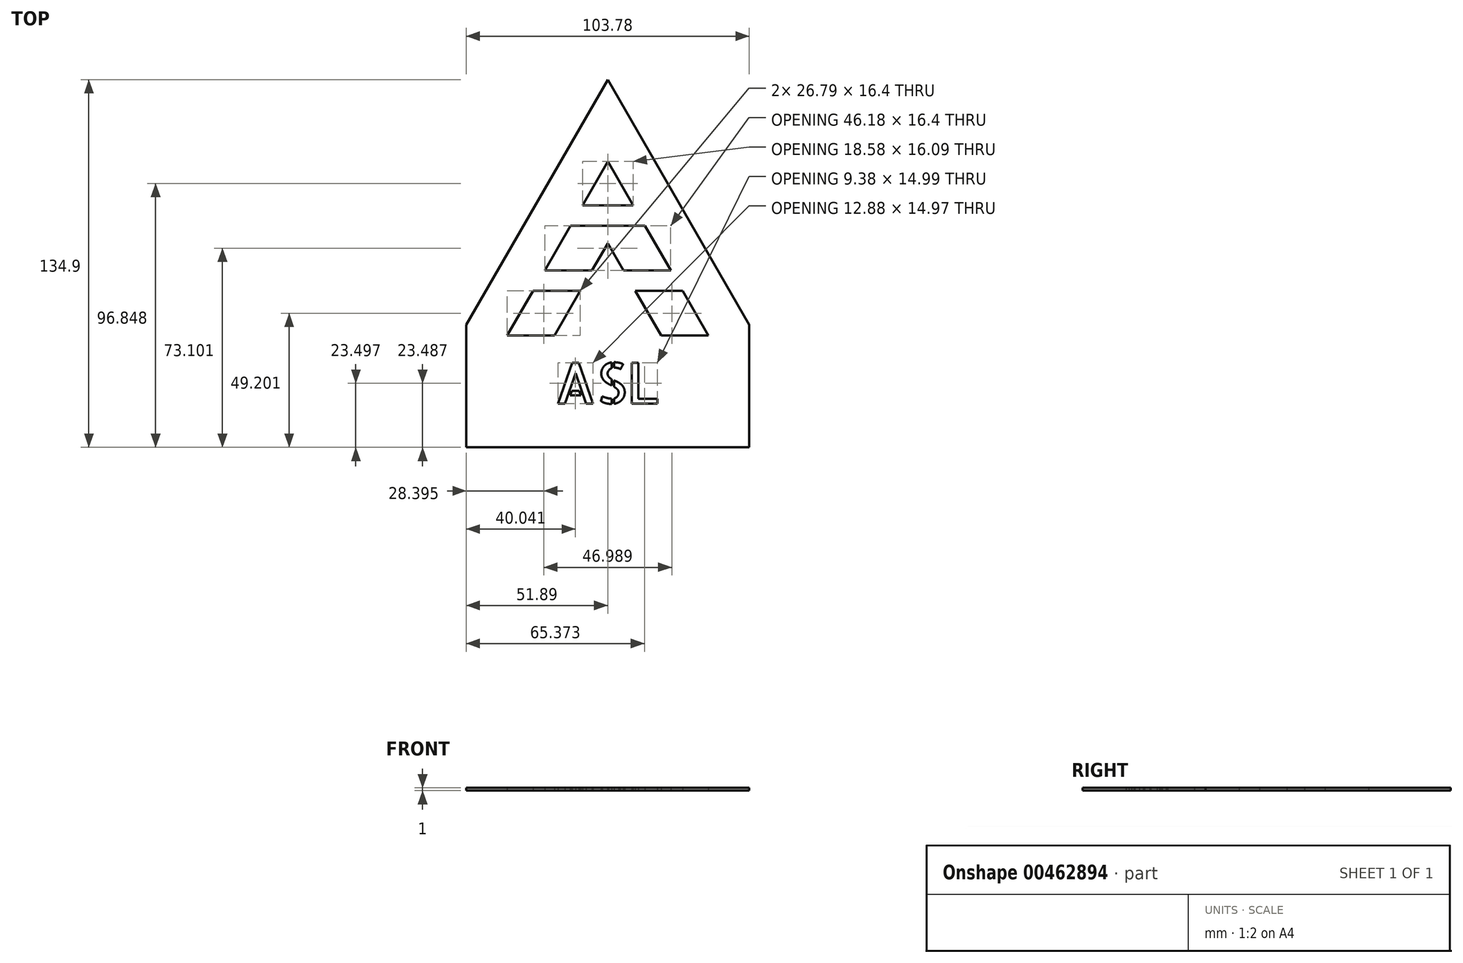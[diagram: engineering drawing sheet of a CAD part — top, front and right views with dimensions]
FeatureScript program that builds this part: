
annotation { "Feature Type Name" : "Feature", "Feature Type Description" : "" }
export const myFeature = defineFeature(function(context is Context, id is Id, definition is map)
    precondition{}
    {
        {
            var Q0;
            Q0=qCreatedBy(makeId("Top.planeOp"),FACE);
            var sketch = newSketch(context, id + "F0", { "sketchPlane" : qUnion([Q0])});
            skLineSegment(sketch, "E0", {"start": v(0, 0) * mm, "end": v(0, -221.26) * mm, "construction": true});
            skLineSegment(sketch, "E1", {"start": v(0, -110.63) * mm, "end": v(159.78, -110.63) * mm, "construction": true});
            skLineSegment(sketch, "E2.MirrorCS", {"start": v(0, -110.63) * mm, "end": v(-159.78, -110.63) * mm, "construction": true});
            skLineSegment(sketch, "E3", {"start": v(-19.57, -100.63) * mm, "end": v(19.57, -100.63) * mm});
            skLineSegment(sketch, "E4", {"start": v(19.57, -100.63) * mm, "end": v(0, -66.73) * mm});
            skLineSegment(sketch, "E5", {"start": v(0, -66.73) * mm, "end": v(-19.57, -100.63) * mm});
            skPoint(sketch, "E6", {"position": v(0, -100.63) * mm});
            skLineSegment(sketch, "E7", {"start": v(0, -110.63) * mm, "end": v(0, -100.63) * mm, "construction": true});
            skText(sketch, "E8", { "text": "ASL", "fontName": "AllertaStencil-Regular.ttf"});
            skLineSegment(sketch, "E9.0", {"start": v(0, -36.73) * mm, "end": v(-32.56, -93.13) * mm});
            skLineSegment(sketch, "E9.1", {"start": v(32.56, -93.13) * mm, "end": v(0, -36.73) * mm});
            skLineSegment(sketch, "E10", {"start": v(-32.56, -93.13) * mm, "end": v(-36.89, -100.63) * mm});
            skLineSegment(sketch, "E11", {"start": v(-36.89, -100.63) * mm, "end": v(-19.57, -100.63) * mm});
            skLineSegment(sketch, "E12.MirrorCS", {"start": v(36.89, -100.63) * mm, "end": v(19.57, -100.63) * mm});
            skLineSegment(sketch, "E13.MirrorCS", {"start": v(32.56, -93.13) * mm, "end": v(36.89, -100.63) * mm});
            skLineSegment(sketch, "E14", {"start": v(0, -100.63) * mm, "end": v(0, -84.23) * mm, "construction": true});
            skLineSegment(sketch, "E15", {"start": v(27.42, -84.23) * mm, "end": v(-27.42, -84.23) * mm});
            skLineSegment(sketch, "E16", {"start": v(0, -84.23) * mm, "end": v(0, -76.73) * mm, "construction": true});
            skLineSegment(sketch, "E17", {"start": v(23.1, -76.73) * mm, "end": v(-23.1, -76.73) * mm});
            skLineSegment(sketch, "E18", {"start": v(0, -76.73) * mm, "end": v(0, -60.33) * mm, "construction": true});
            skLineSegment(sketch, "E19", {"start": v(13.62, -60.33) * mm, "end": v(-13.62, -60.33) * mm});
            skLineSegment(sketch, "E20", {"start": v(0, -60.33) * mm, "end": v(0, -52.83) * mm, "construction": true});
            skLineSegment(sketch, "E21", {"start": v(9.3, -52.83) * mm, "end": v(-9.3, -52.83) * mm});
            skLineSegment(sketch, "E22", {"start": v(0, -125.63) * mm, "end": v(0, -140.63) * mm, "construction": true});
            skLineSegment(sketch, "E23", {"start": v(36.89, -100.63) * mm, "end": v(51.89, -100.63) * mm, "construction": true});
            skLineSegment(sketch, "E24", {"start": v(0, -36.73) * mm, "end": v(0, -21.73) * mm, "construction": true});
            skLineSegment(sketch, "E25", {"start": v(-19.57, -125.63) * mm, "end": v(19.57, -125.63) * mm, "construction": true});
            skLineSegment(sketch, "E26", {"start": v(-19.57, -125.63) * mm, "end": v(-19.57, -126.63) * mm, "construction": true});
            skLineSegment(sketch, "E27", {"start": v(-19.57, -126.63) * mm, "end": v(36.89, -126.63) * mm, "construction": true});
            skLineSegment(sketch, "E28", {"start": v(-19.57, -126.63) * mm, "end": v(-36.89, -126.63) * mm, "construction": true});
            skLineSegment(sketch, "E29", {"start": v(36.89, -100.63) * mm, "end": v(36.89, -126.63) * mm, "construction": true});
            skLineSegment(sketch, "E30", {"start": v(-36.89, -100.63) * mm, "end": v(-36.89, -126.63) * mm, "construction": true});
            skLineSegment(sketch, "E31.0", {"start": v(-19.57, -141.63) * mm, "end": v(51.89, -141.63) * mm});
            skLineSegment(sketch, "E31.1", {"start": v(51.89, -96.6) * mm, "end": v(51.89, -141.63) * mm});
            skLineSegment(sketch, "E31.2", {"start": v(-19.57, -141.63) * mm, "end": v(-51.89, -141.63) * mm});
            skLineSegment(sketch, "E31.3", {"start": v(45.55, -85.63) * mm, "end": v(51.89, -96.6) * mm});
            skLineSegment(sketch, "E31.4", {"start": v(-51.89, -96.6) * mm, "end": v(-51.89, -141.63) * mm});
            skLineSegment(sketch, "E31.5", {"start": v(-45.55, -85.63) * mm, "end": v(-51.89, -96.6) * mm});
            skLineSegment(sketch, "E31.6", {"start": v(0, -6.73) * mm, "end": v(-45.55, -85.63) * mm});
            skLineSegment(sketch, "E31.7", {"start": v(45.55, -85.63) * mm, "end": v(0, -6.73) * mm});
            skLineSegment(sketch, "E32", {"start": v(0, -6.73) * mm, "end": v(0, -140.63) * mm, "construction": true});
            skLineSegment(sketch, "E33", {"start": v(0, -6.73) * mm, "end": v(0, -141.63) * mm, "construction": true});
            skLineSegment(sketch, "E34", {"start": v(-51.89, -141.63) * mm, "end": v(51.89, -141.63) * mm});
            const initialGuessF0  = {"E8": [-0.01957, -0.12563, 1, 0, 0.015]};
            skSetInitialGuess(sketch, initialGuessF0);
            skSolve(sketch);
        }
        {
            var Q0;
            Q0=makeQuery(id+"F0.imprint","IMPRINT",FACE,{"disambiguationData":[TD([[makeQuery(id+"F0.imprint","IMPRINT",EDGE,{"derivedFrom":sQuery(id+"F0.wireOp",EDGE,"E3")}),-1.0]])]});
            var Q1;
            {var subQ0=sQuery(id+"F0.wireOp",EDGE,"E15");var subQ1=sQuery(id+"F0.wireOp",EDGE,"E4");var subQ2=makeQuery(id+"F0.imprint","INTERSECT",VERTEX,{"derivedFrom":[subQ1,subQ0]});Q1=makeQuery(id+"F0.imprint","IMPRINT",FACE,{"disambiguationData":[TD([[makeQuery(id+"F0.imprint","IMPRINT",EDGE,{"disambiguationData":[TD([[subQ2,-1.0]])],"derivedFrom":subQ1}),-1.0]])]});}
            var Q2;
            {var subQ0=sQuery(id+"F0.wireOp",EDGE,"E17");var subQ1=sQuery(id+"F0.wireOp",EDGE,"E5");var subQ2=makeQuery(id+"F0.imprint","INTERSECT",VERTEX,{"derivedFrom":[subQ1,subQ0]});Q2=makeQuery(id+"F0.imprint","IMPRINT",FACE,{"disambiguationData":[TD([[makeQuery(id+"F0.imprint","IMPRINT",EDGE,{"disambiguationData":[TD([[subQ2,-1.0]])],"derivedFrom":subQ1}),-1.0]])]});}
            var Q3;
            {var subQ0=sQuery(id+"F0.wireOp",EDGE,"E15");var subQ1=sQuery(id+"F0.wireOp",EDGE,"E4");var subQ2=makeQuery(id+"F0.imprint","INTERSECT",VERTEX,{"derivedFrom":[subQ1,subQ0]});Q3=makeQuery(id+"F0.imprint","IMPRINT",FACE,{"disambiguationData":[TD([[makeQuery(id+"F0.imprint","IMPRINT",EDGE,{"disambiguationData":[TD([[subQ2,-1.0]])],"derivedFrom":subQ1}),1.0]])]});}
            var Q4;
            {var subQ0=sQuery(id+"F0.wireOp",EDGE,"E3");Q4=makeQuery(id+"F0.imprint","IMPRINT",FACE,{"disambiguationData":[TD([[makeQuery(id+"F0.imprint","IMPRINT",EDGE,{"derivedFrom":subQ0}),1.0]])]});}
            var Q5;
            {var subQ0=sQuery(id+"F0.wireOp",EDGE,"E5");var subQ1=sQuery(id+"F0.wireOp",EDGE,"E4");var subQ2=makeQuery(id+"F0.imprint","INTERSECT",VERTEX,{"derivedFrom":[subQ1,subQ0]});Q5=makeQuery(id+"F0.imprint","IMPRINT",FACE,{"disambiguationData":[TD([[makeQuery(id+"F0.imprint","IMPRINT",EDGE,{"disambiguationData":[TD([[subQ2,1.0]])],"derivedFrom":subQ1}),1.0]])]});}
            var Q6;
            {var subQ0=sQuery(id+"F0.wireOp",EDGE,"E19");Q6=makeQuery(id+"F0.imprint","IMPRINT",FACE,{"disambiguationData":[TD([[makeQuery(id+"F0.imprint","IMPRINT",EDGE,{"derivedFrom":subQ0}),-1.0]])]});}
            extrude(context, id + "F1", {"entities" : qUnion([Q0, Q1, Q2, Q3, Q4, Q5, Q6]), "depth" : 1 * mm});
        }
    });
